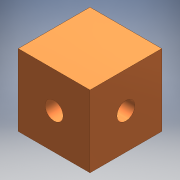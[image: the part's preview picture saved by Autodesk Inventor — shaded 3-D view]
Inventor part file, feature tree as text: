
AUTODESK INVENTOR PART (.ipt)
format: ipt  version: 2016 (Build 200138000, 138)  size: 109,056 bytes
history: native  units: mm
features: other x3, sketch x3, hole x2, extrude x1
ambient origin geometry x8: Origin, YZ Plane, XZ Plane, XY Plane, X Axis, Y Axis, Z Axis, Center Point
bodies: Body1 (feature_tree)
feature tree (9):
  other  "ソリッド1"
  extrude  "押し出し1"  Depth=10.0mm
  hole  "穴1"  [1 undecoded]
  hole  "穴2"  [1 undecoded]
  sketch  "スケッチ1"
  sketch  "スケッチ2"
  sketch  "スケッチ3"
  other  "断面エッジを投影1"
  other  "断面エッジを投影2"
note: 2 required parameter values undecoded (feature->parameter linkage not recoverable at this tier; creation-order binding heuristic only, values carry confidence <= 0.55)
